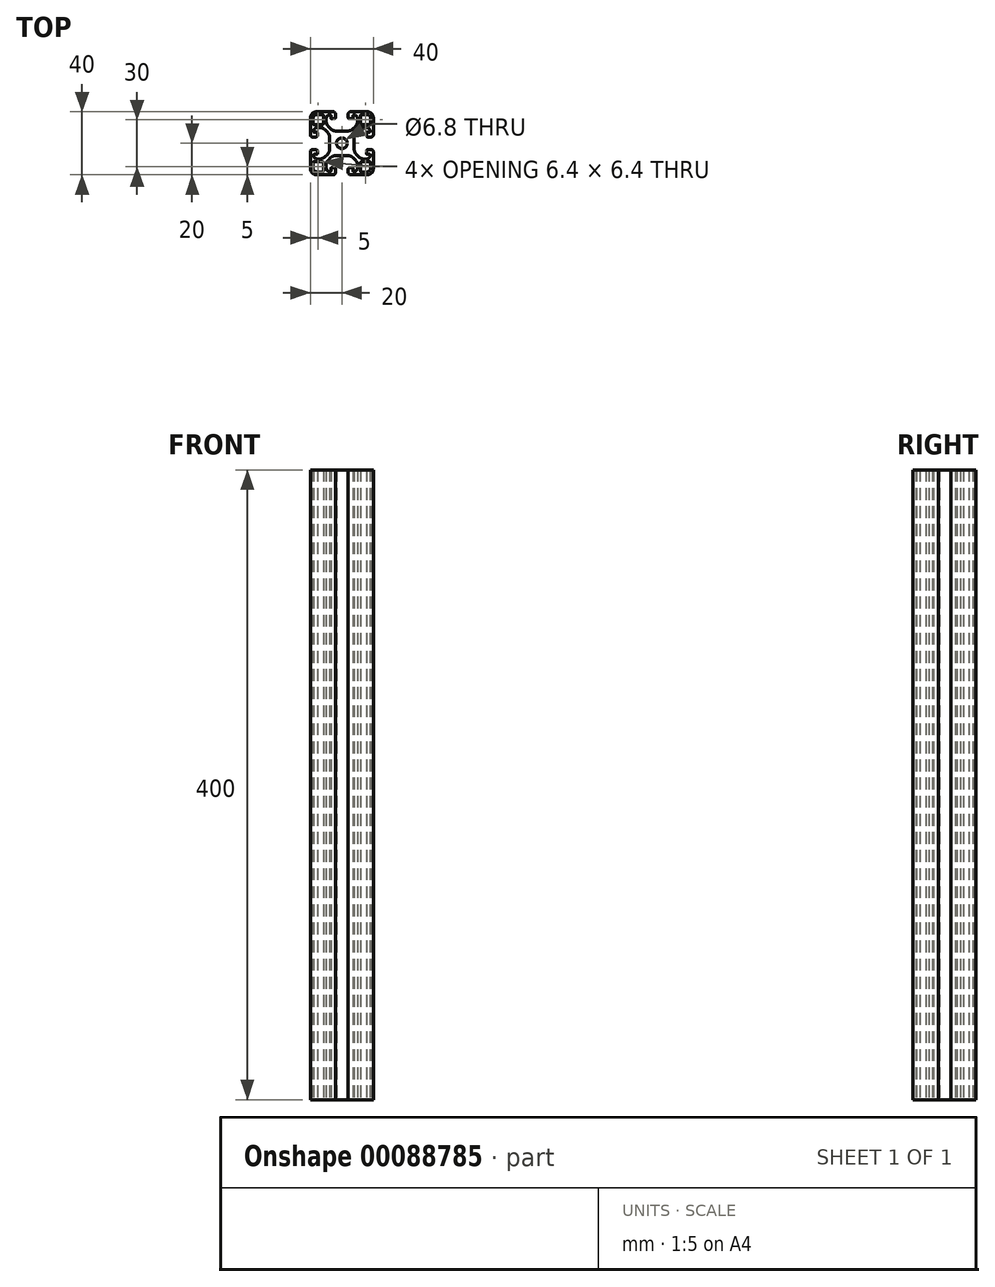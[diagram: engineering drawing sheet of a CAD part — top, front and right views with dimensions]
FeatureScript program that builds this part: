
annotation { "Feature Type Name" : "Feature", "Feature Type Description" : "" }
export const myFeature = defineFeature(function(context is Context, id is Id, definition is map)
    precondition{}
    {
        {
            var Q0;
            Q0=qCreatedBy(makeId("Top.planeOp"),FACE);
            var sketch = newSketch(context, id + "F0", { "sketchPlane" : qUnion([Q0])});
            skLineSegment(sketch, "E0", {"start": v(8.54, -10.66) * mm, "end": v(7.1, -9.21) * mm});
            skLineSegment(sketch, "E1", {"start": v(10.66, -8.54) * mm, "end": v(9.21, -7.1) * mm});
            skLineSegment(sketch, "E2", {"start": v(-9.21, 7.1) * mm, "end": v(-10.66, 8.54) * mm});
            skLineSegment(sketch, "E3", {"start": v(-7.1, 9.21) * mm, "end": v(-8.54, 10.66) * mm});
            skLineSegment(sketch, "E4", {"start": v(-16, -20) * mm, "end": v(-5.5, -20) * mm});
            skLineSegment(sketch, "E5", {"start": v(5.5, -20) * mm, "end": v(16, -20) * mm});
            skLineSegment(sketch, "E6", {"start": v(12.3, -18.2) * mm, "end": v(16, -18.2) * mm});
            skLineSegment(sketch, "E7", {"start": v(-16, -18.2) * mm, "end": v(-12.3, -18.2) * mm});
            skLineSegment(sketch, "E8", {"start": v(-7.5, -18) * mm, "end": v(-7.45, -18) * mm});
            skLineSegment(sketch, "E9", {"start": v(7.45, -18) * mm, "end": v(7.5, -18) * mm});
            skLineSegment(sketch, "E10", {"start": v(-6.5, -15.5) * mm, "end": v(-5, -15.5) * mm});
            skLineSegment(sketch, "E11", {"start": v(5, -15.5) * mm, "end": v(6.5, -15.5) * mm});
            skLineSegment(sketch, "E12", {"start": v(12.3, -11.8) * mm, "end": v(17.7, -11.8) * mm});
            skLineSegment(sketch, "E13", {"start": v(-17.7, -11.8) * mm, "end": v(-12.3, -11.8) * mm});
            skLineSegment(sketch, "E14", {"start": v(14.2, -10) * mm, "end": v(15.5, -10) * mm});
            skLineSegment(sketch, "E15", {"start": v(-15.5, -10) * mm, "end": v(-14.2, -10) * mm});
            skLineSegment(sketch, "E16", {"start": v(-3.56, -7.75) * mm, "end": v(3.56, -7.75) * mm});
            skLineSegment(sketch, "E17", {"start": v(16, -7) * mm, "end": v(17.55, -7) * mm});
            skLineSegment(sketch, "E18", {"start": v(-17.55, -7) * mm, "end": v(-16, -7) * mm});
            skLineSegment(sketch, "E19", {"start": v(-18.5, -4) * mm, "end": v(-16.5, -4) * mm});
            skLineSegment(sketch, "E20", {"start": v(16.5, -4) * mm, "end": v(18.5, -4) * mm});
            skLineSegment(sketch, "E21", {"start": v(16.5, 4) * mm, "end": v(18.5, 4) * mm});
            skLineSegment(sketch, "E22", {"start": v(-18.5, 4) * mm, "end": v(-16.5, 4) * mm});
            skLineSegment(sketch, "E23", {"start": v(16, 7) * mm, "end": v(17.55, 7) * mm});
            skLineSegment(sketch, "E24", {"start": v(-17.55, 7) * mm, "end": v(-16, 7) * mm});
            skLineSegment(sketch, "E25", {"start": v(-3.56, 7.75) * mm, "end": v(3.56, 7.75) * mm});
            skLineSegment(sketch, "E26", {"start": v(14.2, 10) * mm, "end": v(15.5, 10) * mm});
            skLineSegment(sketch, "E27", {"start": v(-15.5, 10) * mm, "end": v(-14.2, 10) * mm});
            skLineSegment(sketch, "E28", {"start": v(-17.7, 11.8) * mm, "end": v(-12.3, 11.8) * mm});
            skLineSegment(sketch, "E29", {"start": v(12.3, 11.8) * mm, "end": v(17.7, 11.8) * mm});
            skLineSegment(sketch, "E30", {"start": v(5, 15.5) * mm, "end": v(6.5, 15.5) * mm});
            skLineSegment(sketch, "E31", {"start": v(-6.5, 15.5) * mm, "end": v(-5, 15.5) * mm});
            skLineSegment(sketch, "E32", {"start": v(7.45, 18) * mm, "end": v(7.5, 18) * mm});
            skLineSegment(sketch, "E33", {"start": v(-7.5, 18) * mm, "end": v(-7.45, 18) * mm});
            skLineSegment(sketch, "E34", {"start": v(-16, 18.2) * mm, "end": v(-12.3, 18.2) * mm});
            skLineSegment(sketch, "E35", {"start": v(12.3, 18.2) * mm, "end": v(16, 18.2) * mm});
            skLineSegment(sketch, "E36", {"start": v(5.5, 20) * mm, "end": v(16, 20) * mm});
            skLineSegment(sketch, "E37", {"start": v(-16, 20) * mm, "end": v(-5.5, 20) * mm});
            skLineSegment(sketch, "E38", {"start": v(-8.54, -10.66) * mm, "end": v(-7.1, -9.21) * mm});
            skLineSegment(sketch, "E39", {"start": v(-10.66, -8.54) * mm, "end": v(-9.21, -7.1) * mm});
            skLineSegment(sketch, "E40", {"start": v(9.21, 7.1) * mm, "end": v(10.66, 8.54) * mm});
            skLineSegment(sketch, "E41", {"start": v(7.1, 9.21) * mm, "end": v(8.54, 10.66) * mm});
            skLineSegment(sketch, "E42", {"start": v(-20, -16) * mm, "end": v(-20, -5.5) * mm});
            skLineSegment(sketch, "E43", {"start": v(-20, 5.5) * mm, "end": v(-20, 16) * mm});
            skLineSegment(sketch, "E44", {"start": v(-18.2, 12.3) * mm, "end": v(-18.2, 16) * mm});
            skLineSegment(sketch, "E45", {"start": v(-18.2, -16) * mm, "end": v(-18.2, -12.3) * mm});
            skLineSegment(sketch, "E46", {"start": v(-18, 7.45) * mm, "end": v(-18, 7.5) * mm});
            skLineSegment(sketch, "E47", {"start": v(-18, -7.5) * mm, "end": v(-18, -7.45) * mm});
            skLineSegment(sketch, "E48", {"start": v(-15.5, 5) * mm, "end": v(-15.5, 6.5) * mm});
            skLineSegment(sketch, "E49", {"start": v(-15.5, -6.5) * mm, "end": v(-15.5, -5) * mm});
            skLineSegment(sketch, "E50", {"start": v(-11.8, 12.3) * mm, "end": v(-11.8, 17.7) * mm});
            skLineSegment(sketch, "E51", {"start": v(-11.8, -17.7) * mm, "end": v(-11.8, -12.3) * mm});
            skLineSegment(sketch, "E52", {"start": v(-10, -15.5) * mm, "end": v(-10, -14.2) * mm});
            skLineSegment(sketch, "E53", {"start": v(-10, 14.2) * mm, "end": v(-10, 15.5) * mm});
            skLineSegment(sketch, "E54", {"start": v(-7.75, -3.56) * mm, "end": v(-7.75, 3.56) * mm});
            skLineSegment(sketch, "E55", {"start": v(-7, -17.55) * mm, "end": v(-7, -16) * mm});
            skLineSegment(sketch, "E56", {"start": v(-7, 16) * mm, "end": v(-7, 17.55) * mm});
            skLineSegment(sketch, "E57", {"start": v(-4, -18.5) * mm, "end": v(-4, -16.5) * mm});
            skLineSegment(sketch, "E58", {"start": v(-4, 16.5) * mm, "end": v(-4, 18.5) * mm});
            skLineSegment(sketch, "E59", {"start": v(4, -18.5) * mm, "end": v(4, -16.5) * mm});
            skLineSegment(sketch, "E60", {"start": v(4, 16.5) * mm, "end": v(4, 18.5) * mm});
            skLineSegment(sketch, "E61", {"start": v(7, -17.55) * mm, "end": v(7, -16) * mm});
            skLineSegment(sketch, "E62", {"start": v(7, 16) * mm, "end": v(7, 17.55) * mm});
            skLineSegment(sketch, "E63", {"start": v(7.75, -3.56) * mm, "end": v(7.75, 3.56) * mm});
            skLineSegment(sketch, "E64", {"start": v(10, -15.5) * mm, "end": v(10, -14.2) * mm});
            skLineSegment(sketch, "E65", {"start": v(10, 14.2) * mm, "end": v(10, 15.5) * mm});
            skLineSegment(sketch, "E66", {"start": v(11.8, 12.3) * mm, "end": v(11.8, 17.7) * mm});
            skLineSegment(sketch, "E67", {"start": v(11.8, -17.7) * mm, "end": v(11.8, -12.3) * mm});
            skLineSegment(sketch, "E68", {"start": v(15.5, -6.5) * mm, "end": v(15.5, -5) * mm});
            skLineSegment(sketch, "E69", {"start": v(15.5, 5) * mm, "end": v(15.5, 6.5) * mm});
            skLineSegment(sketch, "E70", {"start": v(18, -7.5) * mm, "end": v(18, -7.45) * mm});
            skLineSegment(sketch, "E71", {"start": v(18, 7.45) * mm, "end": v(18, 7.5) * mm});
            skLineSegment(sketch, "E72", {"start": v(18.2, 12.3) * mm, "end": v(18.2, 16) * mm});
            skLineSegment(sketch, "E73", {"start": v(18.2, -16) * mm, "end": v(18.2, -12.3) * mm});
            skLineSegment(sketch, "E74", {"start": v(20, -16) * mm, "end": v(20, -5.5) * mm});
            skLineSegment(sketch, "E75", {"start": v(20, 5.5) * mm, "end": v(20, 16) * mm});
            skArc(sketch, "E76", {"start": v(-18.5, -4) * mm, "mid": v(-19.56, -4.44) * mm, "end": v(-20, -5.5) * mm});
            skArc(sketch, "E77", {"start": v(-20, 5.5) * mm, "mid": v(-19.56, 4.44) * mm, "end": v(-18.5, 4) * mm});
            skArc(sketch, "E78", {"start": v(-17.7, -11.8) * mm, "mid": v(-18.05, -11.95) * mm, "end": v(-18.2, -12.3) * mm});
            skArc(sketch, "E79", {"start": v(-18.2, 12.3) * mm, "mid": v(-18.05, 11.95) * mm, "end": v(-17.7, 11.8) * mm});
            skArc(sketch, "E80", {"start": v(-17.55, -7) * mm, "mid": v(-17.87, -7.13) * mm, "end": v(-18, -7.45) * mm});
            skArc(sketch, "E81", {"start": v(-18, 7.45) * mm, "mid": v(-17.87, 7.13) * mm, "end": v(-17.55, 7) * mm});
            skArc(sketch, "E82", {"start": v(-15.5, -5) * mm, "mid": v(-15.8, -4.3) * mm, "end": v(-16.5, -4) * mm});
            skArc(sketch, "E83", {"start": v(-16.5, 4) * mm, "mid": v(-15.8, 4.3) * mm, "end": v(-15.5, 5) * mm});
            skArc(sketch, "E84", {"start": v(-18.2, -16) * mm, "mid": v(-17.56, -17.56) * mm, "end": v(-16, -18.2) * mm});
            skArc(sketch, "E85", {"start": v(-20, -16) * mm, "mid": v(-18.83, -18.83) * mm, "end": v(-16, -20) * mm});
            skArc(sketch, "E86", {"start": v(-16, -7) * mm, "mid": v(-15.65, -6.85) * mm, "end": v(-15.5, -6.5) * mm});
            skArc(sketch, "E87", {"start": v(-15.5, 6.5) * mm, "mid": v(-15.65, 6.85) * mm, "end": v(-16, 7) * mm});
            skArc(sketch, "E88", {"start": v(-16, 18.2) * mm, "mid": v(-17.56, 17.56) * mm, "end": v(-18.2, 16) * mm});
            skArc(sketch, "E89", {"start": v(-16, 20) * mm, "mid": v(-18.83, 18.83) * mm, "end": v(-20, 16) * mm});
            skArc(sketch, "E90", {"start": v(-18, -7.5) * mm, "mid": v(-17.27, -9.27) * mm, "end": v(-15.5, -10) * mm});
            skArc(sketch, "E91", {"start": v(-15.5, 10) * mm, "mid": v(-17.27, 9.27) * mm, "end": v(-18, 7.5) * mm});
            skArc(sketch, "E92", {"start": v(-14.2, -10) * mm, "mid": v(-12.28, -9.62) * mm, "end": v(-10.66, -8.54) * mm});
            skArc(sketch, "E93", {"start": v(-10.66, 8.54) * mm, "mid": v(-12.28, 9.62) * mm, "end": v(-14.2, 10) * mm});
            skArc(sketch, "E94", {"start": v(-9.21, -7.1) * mm, "mid": v(-8.13, -5.47) * mm, "end": v(-7.75, -3.56) * mm});
            skArc(sketch, "E95", {"start": v(-7.75, 3.56) * mm, "mid": v(-8.13, 5.47) * mm, "end": v(-9.21, 7.1) * mm});
            skArc(sketch, "E96", {"start": v(-12.3, -18.2) * mm, "mid": v(-11.95, -18.05) * mm, "end": v(-11.8, -17.7) * mm});
            skArc(sketch, "E97", {"start": v(-11.8, -12.3) * mm, "mid": v(-11.95, -11.95) * mm, "end": v(-12.3, -11.8) * mm});
            skArc(sketch, "E98", {"start": v(-12.3, 11.8) * mm, "mid": v(-11.95, 11.95) * mm, "end": v(-11.8, 12.3) * mm});
            skArc(sketch, "E99", {"start": v(-11.8, 17.7) * mm, "mid": v(-11.95, 18.05) * mm, "end": v(-12.3, 18.2) * mm});
            skArc(sketch, "E100", {"start": v(-10, -15.5) * mm, "mid": v(-9.27, -17.27) * mm, "end": v(-7.5, -18) * mm});
            skArc(sketch, "E101", {"start": v(-7.5, 18) * mm, "mid": v(-9.27, 17.27) * mm, "end": v(-10, 15.5) * mm});
            skArc(sketch, "E102", {"start": v(-7.45, -18) * mm, "mid": v(-7.13, -17.87) * mm, "end": v(-7, -17.55) * mm});
            skArc(sketch, "E103", {"start": v(-7, 17.55) * mm, "mid": v(-7.13, 17.87) * mm, "end": v(-7.45, 18) * mm});
            skArc(sketch, "E104", {"start": v(-6.5, -15.5) * mm, "mid": v(-6.85, -15.65) * mm, "end": v(-7, -16) * mm});
            skArc(sketch, "E105", {"start": v(-7, 16) * mm, "mid": v(-6.85, 15.65) * mm, "end": v(-6.5, 15.5) * mm});
            skArc(sketch, "E106", {"start": v(-5.5, -20) * mm, "mid": v(-4.44, -19.56) * mm, "end": v(-4, -18.5) * mm});
            skArc(sketch, "E107", {"start": v(-4, 18.5) * mm, "mid": v(-4.44, 19.56) * mm, "end": v(-5.5, 20) * mm});
            skArc(sketch, "E108", {"start": v(-4, -16.5) * mm, "mid": v(-4.3, -15.8) * mm, "end": v(-5, -15.5) * mm});
            skArc(sketch, "E109", {"start": v(-8.54, -10.66) * mm, "mid": v(-9.62, -12.28) * mm, "end": v(-10, -14.2) * mm});
            skArc(sketch, "E110", {"start": v(-10, 14.2) * mm, "mid": v(-9.62, 12.28) * mm, "end": v(-8.54, 10.66) * mm});
            skArc(sketch, "E111", {"start": v(-5, 15.5) * mm, "mid": v(-4.3, 15.8) * mm, "end": v(-4, 16.5) * mm});
            skArc(sketch, "E112", {"start": v(-3.56, -7.75) * mm, "mid": v(-5.47, -8.13) * mm, "end": v(-7.1, -9.21) * mm});
            skArc(sketch, "E113", {"start": v(-7.1, 9.21) * mm, "mid": v(-5.47, 8.13) * mm, "end": v(-3.56, 7.75) * mm});
            skCircle(sketch, "E114", {"center": v(0, 0) * mm, "radius": 3.4 * mm});
            skArc(sketch, "E115", {"start": v(7.1, -9.21) * mm, "mid": v(5.47, -8.13) * mm, "end": v(3.56, -7.75) * mm});
            skArc(sketch, "E116", {"start": v(3.56, 7.75) * mm, "mid": v(5.47, 8.13) * mm, "end": v(7.1, 9.21) * mm});
            skArc(sketch, "E117", {"start": v(5, -15.5) * mm, "mid": v(4.3, -15.8) * mm, "end": v(4, -16.5) * mm});
            skArc(sketch, "E118", {"start": v(10, -14.2) * mm, "mid": v(9.62, -12.28) * mm, "end": v(8.54, -10.66) * mm});
            skArc(sketch, "E119", {"start": v(8.54, 10.66) * mm, "mid": v(9.62, 12.28) * mm, "end": v(10, 14.2) * mm});
            skArc(sketch, "E120", {"start": v(4, 16.5) * mm, "mid": v(4.3, 15.8) * mm, "end": v(5, 15.5) * mm});
            skArc(sketch, "E121", {"start": v(4, -18.5) * mm, "mid": v(4.44, -19.56) * mm, "end": v(5.5, -20) * mm});
            skArc(sketch, "E122", {"start": v(5.5, 20) * mm, "mid": v(4.44, 19.56) * mm, "end": v(4, 18.5) * mm});
            skArc(sketch, "E123", {"start": v(7, -16) * mm, "mid": v(6.85, -15.65) * mm, "end": v(6.5, -15.5) * mm});
            skArc(sketch, "E124", {"start": v(6.5, 15.5) * mm, "mid": v(6.85, 15.65) * mm, "end": v(7, 16) * mm});
            skArc(sketch, "E125", {"start": v(7, -17.55) * mm, "mid": v(7.13, -17.87) * mm, "end": v(7.45, -18) * mm});
            skArc(sketch, "E126", {"start": v(7.45, 18) * mm, "mid": v(7.13, 17.87) * mm, "end": v(7, 17.55) * mm});
            skArc(sketch, "E127", {"start": v(7.5, -18) * mm, "mid": v(9.27, -17.27) * mm, "end": v(10, -15.5) * mm});
            skArc(sketch, "E128", {"start": v(10, 15.5) * mm, "mid": v(9.27, 17.27) * mm, "end": v(7.5, 18) * mm});
            skArc(sketch, "E129", {"start": v(11.8, -17.7) * mm, "mid": v(11.95, -18.05) * mm, "end": v(12.3, -18.2) * mm});
            skArc(sketch, "E130", {"start": v(12.3, -11.8) * mm, "mid": v(11.95, -11.95) * mm, "end": v(11.8, -12.3) * mm});
            skArc(sketch, "E131", {"start": v(11.8, 12.3) * mm, "mid": v(11.95, 11.95) * mm, "end": v(12.3, 11.8) * mm});
            skArc(sketch, "E132", {"start": v(12.3, 18.2) * mm, "mid": v(11.95, 18.05) * mm, "end": v(11.8, 17.7) * mm});
            skArc(sketch, "E133", {"start": v(7.75, -3.56) * mm, "mid": v(8.13, -5.47) * mm, "end": v(9.21, -7.1) * mm});
            skArc(sketch, "E134", {"start": v(9.21, 7.1) * mm, "mid": v(8.13, 5.47) * mm, "end": v(7.75, 3.56) * mm});
            skArc(sketch, "E135", {"start": v(10.66, -8.54) * mm, "mid": v(12.28, -9.62) * mm, "end": v(14.2, -10) * mm});
            skArc(sketch, "E136", {"start": v(14.2, 10) * mm, "mid": v(12.28, 9.62) * mm, "end": v(10.66, 8.54) * mm});
            skArc(sketch, "E137", {"start": v(15.5, -10) * mm, "mid": v(17.27, -9.27) * mm, "end": v(18, -7.5) * mm});
            skArc(sketch, "E138", {"start": v(18, 7.5) * mm, "mid": v(17.27, 9.27) * mm, "end": v(15.5, 10) * mm});
            skArc(sketch, "E139", {"start": v(16, -18.2) * mm, "mid": v(17.56, -17.56) * mm, "end": v(18.2, -16) * mm});
            skArc(sketch, "E140", {"start": v(16, -20) * mm, "mid": v(18.83, -18.83) * mm, "end": v(20, -16) * mm});
            skArc(sketch, "E141", {"start": v(15.5, -6.5) * mm, "mid": v(15.65, -6.85) * mm, "end": v(16, -7) * mm});
            skArc(sketch, "E142", {"start": v(16, 7) * mm, "mid": v(15.65, 6.85) * mm, "end": v(15.5, 6.5) * mm});
            skArc(sketch, "E143", {"start": v(18.2, 16) * mm, "mid": v(17.56, 17.56) * mm, "end": v(16, 18.2) * mm});
            skArc(sketch, "E144", {"start": v(20, 16) * mm, "mid": v(18.83, 18.83) * mm, "end": v(16, 20) * mm});
            skArc(sketch, "E145", {"start": v(16.5, -4) * mm, "mid": v(15.8, -4.3) * mm, "end": v(15.5, -5) * mm});
            skArc(sketch, "E146", {"start": v(15.5, 5) * mm, "mid": v(15.8, 4.3) * mm, "end": v(16.5, 4) * mm});
            skArc(sketch, "E147", {"start": v(18, -7.45) * mm, "mid": v(17.87, -7.13) * mm, "end": v(17.55, -7) * mm});
            skArc(sketch, "E148", {"start": v(17.55, 7) * mm, "mid": v(17.87, 7.13) * mm, "end": v(18, 7.45) * mm});
            skArc(sketch, "E149", {"start": v(18.2, -12.3) * mm, "mid": v(18.05, -11.95) * mm, "end": v(17.7, -11.8) * mm});
            skArc(sketch, "E150", {"start": v(17.7, 11.8) * mm, "mid": v(18.05, 11.95) * mm, "end": v(18.2, 12.3) * mm});
            skArc(sketch, "E151", {"start": v(20, -5.5) * mm, "mid": v(19.56, -4.44) * mm, "end": v(18.5, -4) * mm});
            skArc(sketch, "E152", {"start": v(18.5, 4) * mm, "mid": v(19.56, 4.44) * mm, "end": v(20, 5.5) * mm});
            skLineSegment(sketch, "E153", {"start": v(0, 20) * mm, "end": v(0, -20) * mm});
            skLineSegment(sketch, "E154", {"start": v(-20, 0) * mm, "end": v(20, 0) * mm});
            skSolve(sketch);
        }
        {
            var Q0;
            Q0=qSketchRegion(id+"F0",true);
            extrude(context, id + "F1", {"entities" : qUnion([Q0]), "depth" : 400 * mm});
        }
    });
